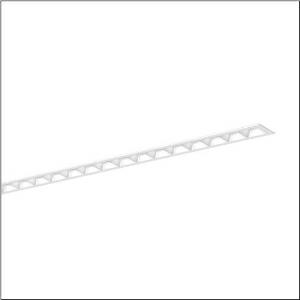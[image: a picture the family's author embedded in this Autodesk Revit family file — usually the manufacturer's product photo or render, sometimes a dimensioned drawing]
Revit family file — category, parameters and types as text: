
# Revit family: silica_r__21_51mx16db35wb_6bb0
name_source: partatom
category: Lighting Fixtures
units: mm (PartAtom-declared; Revit-internal decimal feet)

## family parameters
Cut with Voids When Loaded = No
Host = Face
Light Source = No
Part Type = Normal
Room Calculation Point = No
Round Connector Dimension = Use Diameter
Shared = No

## types (1)
- --- (1 x LED, 5400 lm, 31.4 W, 3000K)
    Apparent Load = 31 VA
    CIE Flux Codes = 83 98 100 100 100
    Color Rendering = 80
    Color Temperature = 3000K
    Default Elevation = 1800 mm
    Description = Silica® 21, office luminaire, primary light control with darklight reflector, of PMMA, white, CAT 2 (L<= 3000cd/m²), light emission: direct distribution, primary light characteristic: symmetric, installation type: recessed, LED, rated luminous flux: 5.400lm, luminous efficacy: 172lm/W, light colour: 830, colour temperature: 3000K, control gear: DALI 2, with terminal, 3+2-pole, max. 2.5mm², mains connection: 220..240V, AC, 50/60Hz, rated input power: 31.4W, luminaire housing, of aluminium, traffic white (RAL 9016), length: 1.528mm, width: 79mm, height: 53mm, protection rating (complete): IP20, insulation class (complete): insulation class I (protective earthing), certification: CE, ENEC, VDE, permissible operating ambient temperature: 0..+35°C, standard: EN 50419, packaging unit: 1 piece
    Height = 0 mm  [stored 0 ft]
    Lamp = 1 x LED
    Lamp Light Flux = 5400 lm
    Lamp Power = 31.4 W
    Lamp count = 1
    Length = 1527 mm
    Luminous efficacy = 172 lm/W
    Manufacturer = Siteco
    ModVariant = No
    Model = 51MX16DB35WB
    Mounting Place = Ceiling
    Mounting Type = Recessed
    Number of Poles = 1
    OnlyDefault = Yes
    Power Factor = 1
    Product Name = Silica® 21
    Product group = office luminaire | ceiling recessed
    ProductGroupID = 401
    Protection Class = Protection class I
    Protection Degree = IP 20
    RLX_Detail_Level = 1
    RLX_Emergency_Light_Flux = 0 lm
    RLX_Emergency_Type = 0
    RLX_Emergency_Type_DB = No
    RlxData = <blob elided: 39853 chars, md5=65a884ca>
    Socket = socket
    Standby Power = 0 W
    System Light Flux = 5400 lm
    System Power = 31 W
    Type Comments = factory setting: luminous flux: 100 % | dim-lin: 254 | 360 mA
    Type Image = l_1335884.jpg
    URL = http://relux.com
    VarID = @adj_124084
    Voltage = 0 V
    Weight = 0.00 kg
    Width = 79 mm

note: [stored X ft] marks values corroborated as IEEE doubles in the binary element streams (Revit-internal decimal feet)

## geometry (parser evidence)
native form markers: Blend x4, Sweep x10
no freeform markers — native parametric forms only
